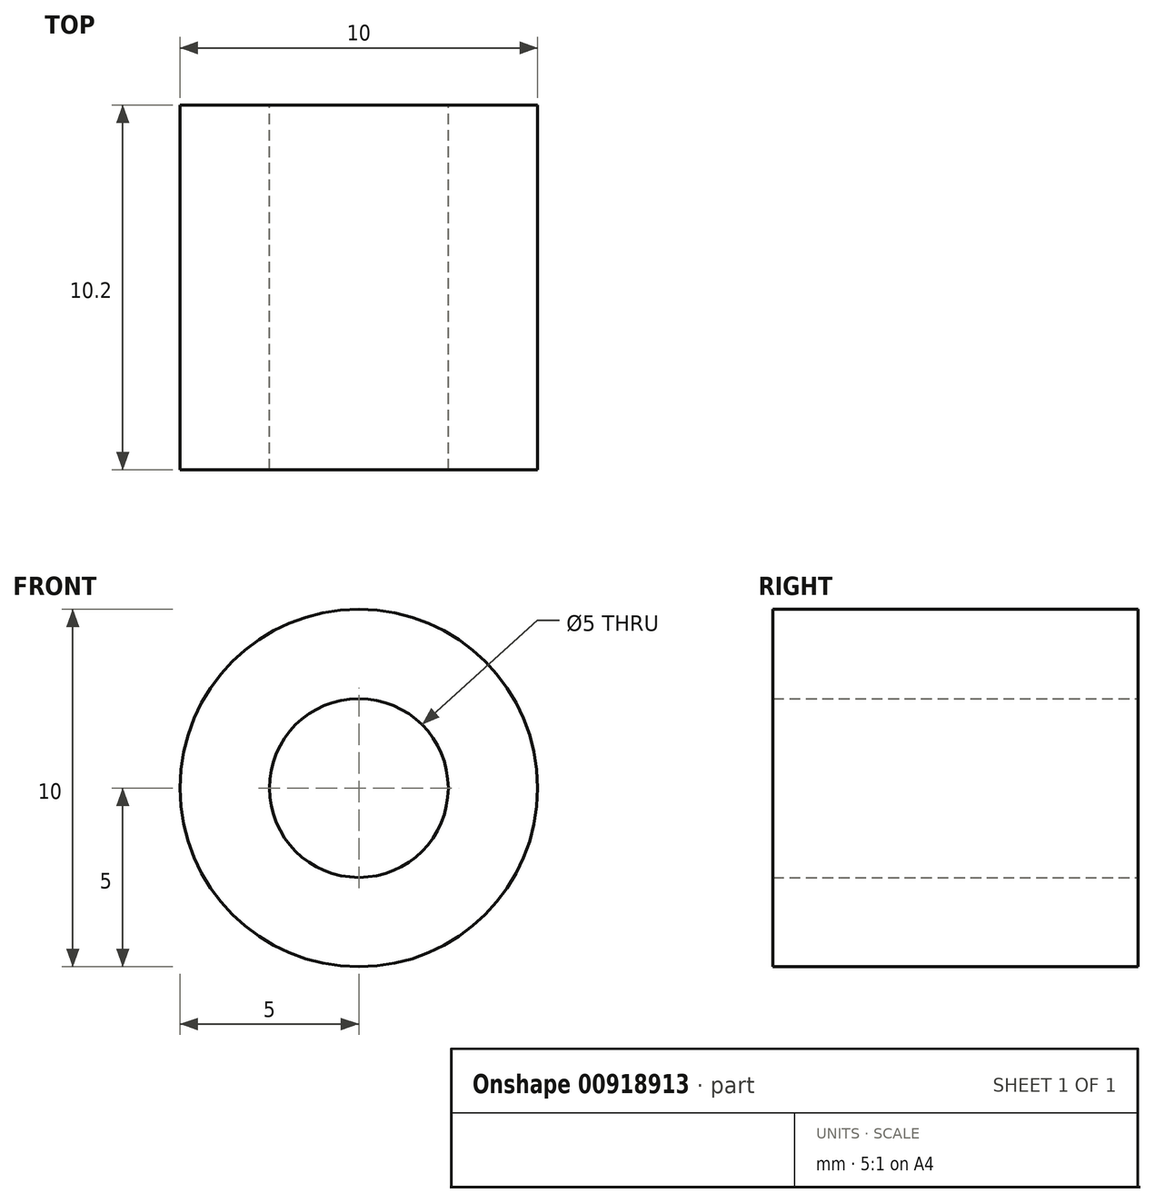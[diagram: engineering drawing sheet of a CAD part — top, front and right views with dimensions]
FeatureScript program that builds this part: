
annotation { "Feature Type Name" : "Feature", "Feature Type Description" : "" }
export const myFeature = defineFeature(function(context is Context, id is Id, definition is map)
    precondition{}
    {
        {
            var Q0;
            Q0=qCreatedBy(makeId("Front.planeOp"),FACE);
            var sketch = newSketch(context, id + "F0", { "sketchPlane" : qUnion([Q0])});
            skCircle(sketch, "E0", {"center": v(0, 0) * mm, "radius": 5 * mm});
            skCircle(sketch, "E1", {"center": v(0, 0) * mm, "radius": 2.5 * mm});
            skSolve(sketch);
        }
        {
            var Q0;
            Q0 = qSketchRegion(id + "F0", true);
            extrude(context, id + "F1", {"entities" : qUnion([Q0]), "depth" : 10.2 * mm, "offsetDistance" : 25 * mm});
        }
    });
